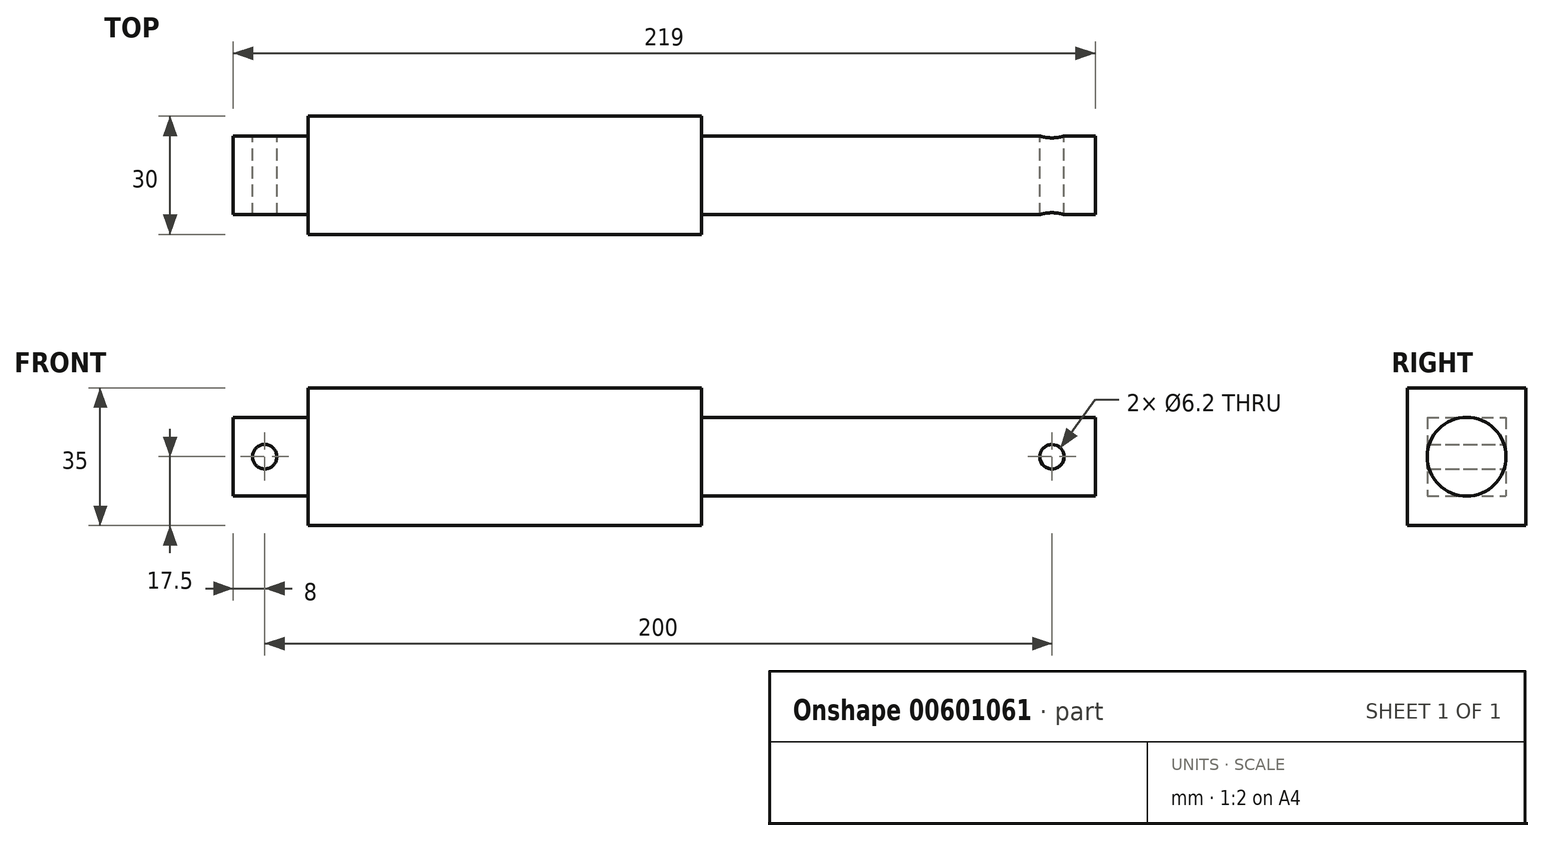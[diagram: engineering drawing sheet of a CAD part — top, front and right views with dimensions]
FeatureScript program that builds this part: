
annotation { "Feature Type Name" : "Feature", "Feature Type Description" : "" }
export const myFeature = defineFeature(function(context is Context, id is Id, definition is map)
    precondition{}
    {
        {
            var Q0;
            Q0=qCreatedBy(makeId("Front.planeOp"),FACE);
            var sketch = newSketch(context, id + "F0", { "sketchPlane" : qUnion([Q0])});
            skLineSegment(sketch, "E0", {"start": v(-60, 0) * mm, "end": v(60, 0) * mm, "construction": true});
            skCircle(sketch, "E1", {"center": v(-60, 0) * mm, "radius": 3.1 * mm});
            skCircle(sketch, "E2", {"center": v(60, 0) * mm, "radius": 3.1 * mm});
            skLineSegment(sketch, "E3", {"start": v(-60, 0) * mm, "end": v(-49, 0) * mm, "construction": true});
            skLineSegment(sketch, "E4", {"start": v(-49, 10) * mm, "end": v(-49, -10) * mm});
            skLineSegment(sketch, "E5", {"start": v(-49, 10) * mm, "end": v(-68, 10) * mm});
            skLineSegment(sketch, "E6", {"start": v(-68, 10) * mm, "end": v(-68, -10) * mm});
            skLineSegment(sketch, "E7", {"start": v(-68, -10) * mm, "end": v(-49, -10) * mm});
            skLineSegment(sketch, "E8", {"start": v(-49, 17.5) * mm, "end": v(-49, -17.5) * mm});
            skLineSegment(sketch, "E9", {"start": v(-49, 17.5) * mm, "end": v(51, 17.5) * mm});
            skLineSegment(sketch, "E10", {"start": v(51, 17.5) * mm, "end": v(51, -17.5) * mm});
            skLineSegment(sketch, "E11", {"start": v(51, -17.5) * mm, "end": v(-49, -17.5) * mm});
            skSolve(sketch);
        }
        {
            var Q0;
            Q0=makeQuery(id+"F0.imprint","IMPRINT",FACE,{"disambiguationData":[TD([[makeQuery(id+"F0.imprint","IMPRINT",EDGE,{"derivedFrom":sQuery(id+"F0.wireOp",EDGE,"E1")}),-1.0]])]});
            extrude(context, id + "F1", {"entities" : qUnion([Q0]), "endBound" : BoundingType.SYMMETRIC, "depth" : 20 * mm, "offsetDistance" : 25 * mm});
        }
        {
            var Q0;
            {var subQ0=sQuery(id+"F0.wireOp",EDGE,"E9");Q0=makeQuery(id+"F0.imprint","IMPRINT",FACE,{"disambiguationData":[TD([[makeQuery(id+"F0.imprint","IMPRINT",EDGE,{"derivedFrom":subQ0}),-1.0]])]});}
            extrude(context, id + "F2", {"entities" : qUnion([Q0]), "operationType" : NewBodyOperationType.ADD, "endBound" : BoundingType.SYMMETRIC, "depth" : 30 * mm, "offsetDistance" : 25 * mm});
        }
        {
            var Q0;
            Q0=makeQuery(id+"F2.opExtrude","SWEPT_FACE",FACE,{"disambiguationData":[OSD([sQuery(id+"F0.wireOp",EDGE,"E10")])]});
            cPlane(context, id + "F3", {"entities" : qUnion([Q0]), "cplaneType" : CPlaneType.OFFSET, "offset" : 0 * mm, "width" : 150 * mm, "height" : 150 * mm});
        }
        {
            var Q0;
            Q0=qCreatedBy(id+"F3.planeOp",FACE);
            var sketch = newSketch(context, id + "F4", { "sketchPlane" : qUnion([Q0])});
            skCircle(sketch, "E12", {"center": v(0, 0) * mm, "radius": 10 * mm});
            skSolve(sketch);
        }
        {
            var Q0;
            Q0 = qSketchRegion(id + "F4", true);
            extrude(context, id + "F5", {"entities" : qUnion([Q0]), "depth" : 100 * mm, "offsetDistance" : 25 * mm});
        }
        {
            var Q0;
            Q0=makeQuery(id+"F5.opExtrude","SWEPT_FACE",FACE,{"disambiguationData":[OSD([sQuery(id+"F4.wireOp",EDGE,"E12")])]});
            cPlane(context, id + "F6", {"entities" : qUnion([Q0]), "cplaneType" : CPlaneType.LINE_ANGLE, "offset" : 25 * mm, "angle" : 0 * degree, "width" : 150 * mm, "height" : 150 * mm});
        }
        {
            var Q0;
            Q0=qCreatedBy(id+"F6.planeOp",FACE);
            var sketch = newSketch(context, id + "F7", { "sketchPlane" : qUnion([Q0])});
            skCircle(sketch, "E13", {"center": v(140, 0) * mm, "radius": 3.1 * mm});
            skSolve(sketch);
        }
        {
            var Q0;
            Q0=makeQuery(id+"F7.imprint","IMPRINT",FACE,{"disambiguationData":[TD([[makeQuery(id+"F7.imprint","IMPRINT",EDGE,{"derivedFrom":sQuery(id+"F7.wireOp",EDGE,"E13")}),1.0]])]});
            var Q1;
            Q1=sQuery(id+"F7.wireOp",EDGE,"E13");
            var Q2;
            Q2=makeQuery(id+"F5.opExtrude","SWEPT_FACE",FACE,{"disambiguationData":[OSD([sQuery(id+"F4.wireOp",EDGE,"E12")])]});
            extrude(context, id + "F8", {"entities" : qUnion([Q0]), "operationType" : NewBodyOperationType.REMOVE, "surfaceEntities" : qUnion([Q1]), "endBound" : BoundingType.SYMMETRIC, "depth" : 20 * mm, "endBoundEntityFace" : qUnion([Q2]), "offsetDistance" : 25 * mm});
        }
    });
